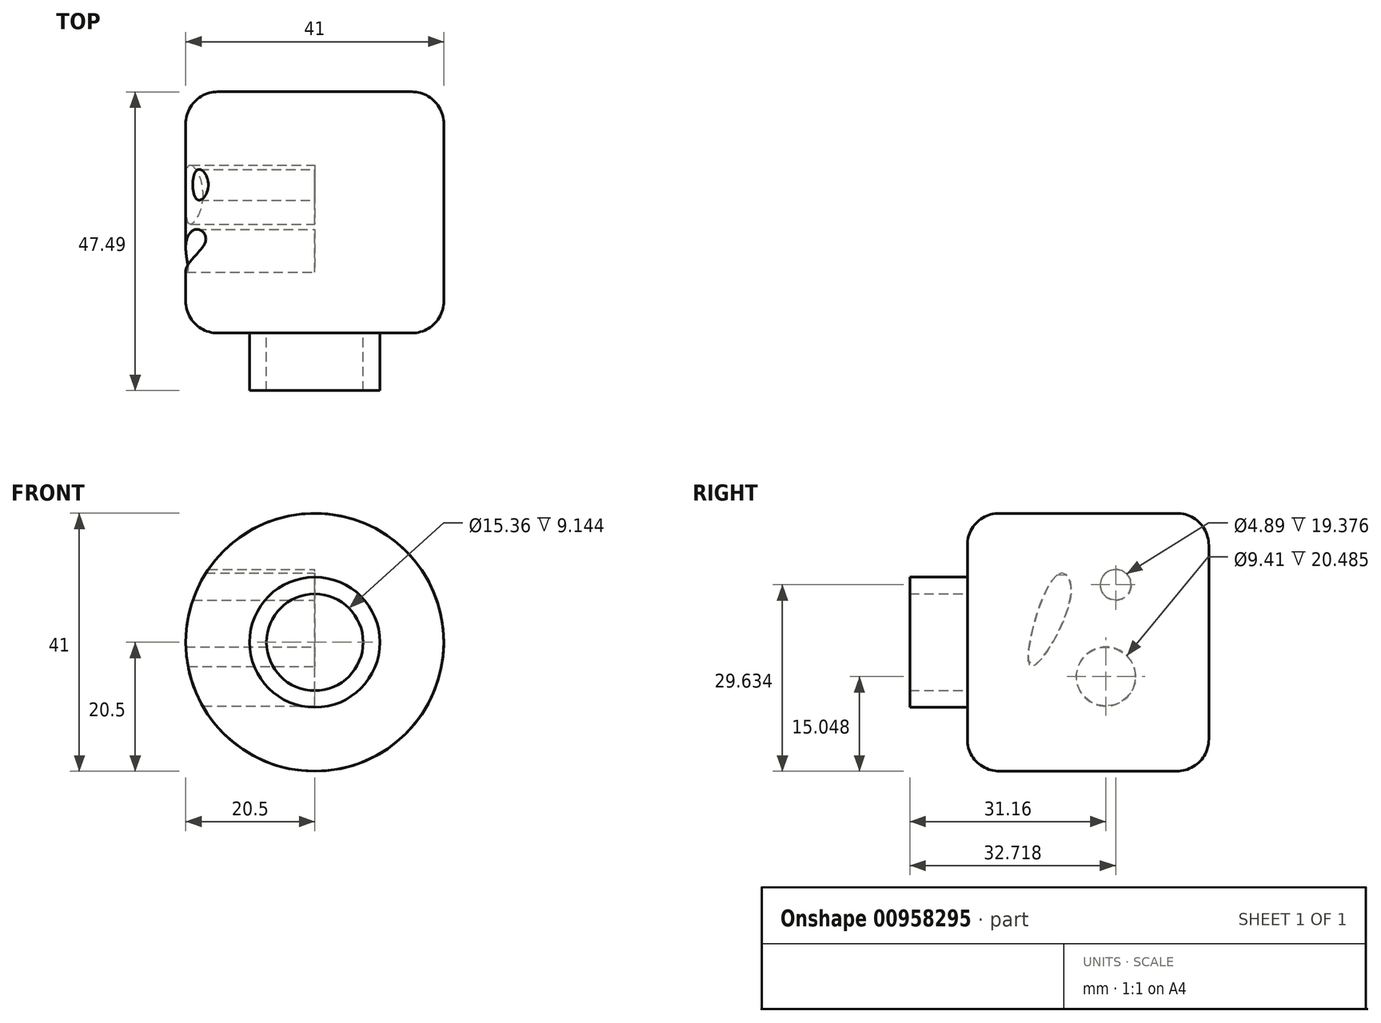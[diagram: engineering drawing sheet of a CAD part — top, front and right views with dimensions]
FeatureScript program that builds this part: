
annotation { "Feature Type Name" : "Feature", "Feature Type Description" : "" }
export const myFeature = defineFeature(function(context is Context, id is Id, definition is map)
    precondition{}
    {
        {
            var Q0;
            Q0=qCreatedBy(makeId("Front.planeOp"),FACE);
            var sketch = newSketch(context, id + "F0", { "sketchPlane" : qUnion([Q0])});
            skCircle(sketch, "E0", {"center": v(0, 0) * mm, "radius": 20.5 * mm});
            skSolve(sketch);
        }
        {
            var Q0;
            Q0=makeQuery(id+"F0.imprint","IMPRINT",FACE,{"disambiguationData":[TD([[makeQuery(id+"F0.imprint","IMPRINT",EDGE,{"derivedFrom":sQuery(id+"F0.wireOp",EDGE,"E0")}),1.0]])]});
            extrude(context, id + "F1", {"entities" : qUnion([Q0]), "oppositeDirection" : true, "depth" : 38.35 * mm, "offsetDistance" : 25.4 * mm});
        }
        {
            var Q0;
            Q0=makeQuery(id+"F1.opExtrude","CAP_EDGE",EDGE,{"disambiguationData":[OSD([sQuery(id+"F0.wireOp",EDGE,"E0")])],"isStart":true});
            var Q1;
            Q1=makeQuery(id+"F1.opExtrude","CAP_EDGE",EDGE,{"disambiguationData":[OSD([sQuery(id+"F0.wireOp",EDGE,"E0")])],"isStart":false});
            fillet(context, id + "F2", {"entities" : qUnion([Q0, Q1]), "radius" : 5.08 * mm, "tangentPropagation" : true, "allowEdgeOverflow" : false});
        }
        {
            var Q0;
            Q0=qCreatedBy(makeId("Front.planeOp"),FACE);
            var sketch = newSketch(context, id + "F3", { "sketchPlane" : qUnion([Q0])});
            skCircle(sketch, "E1", {"center": v(0, 0) * mm, "radius": 10.35 * mm});
            skSolve(sketch);
        }
        {
            var Q0;
            Q0 = qSketchRegion(id + "F3", true);
            extrude(context, id + "F4", {"entities" : qUnion([Q0]), "operationType" : NewBodyOperationType.ADD, "depth" : 9.14 * mm, "offsetDistance" : 25.4 * mm});
        }
        {
            var Q0;
            Q0=qCreatedBy(makeId("Front.planeOp"),FACE);
            var sketch = newSketch(context, id + "F5", { "sketchPlane" : qUnion([Q0])});
            skCircle(sketch, "E2", {"center": v(0, 0) * mm, "radius": 7.68 * mm});
            skSolve(sketch);
        }
        {
            var Q0;
            Q0 = qSketchRegion(id + "F5", true);
            var Q1;
            Q1=makeQuery(id+"F4.opExtrude","CAP_FACE",FACE,{"disambiguationData":[OSD([sQuery(id+"F3.wireOp",EDGE,"E1")])],"isStart":false});
            extrude(context, id + "F6", {"entities" : qUnion([Q0, Q1]), "operationType" : NewBodyOperationType.REMOVE, "depth" : 20.07 * mm, "offsetDistance" : 25.4 * mm});
        }
        {
            var Q0;
            Q0=qCreatedBy(makeId("Right.planeOp"),FACE);
            var sketch = newSketch(context, id + "F7", { "sketchPlane" : qUnion([Q0])});
            skCircle(sketch, "E3", {"center": v(23.58, 9.13) * mm, "radius": 2.44 * mm});
            skCircle(sketch, "E4", {"center": v(22.02, -5.45) * mm, "radius": 4.7 * mm});
            skFitSpline(sketch, "E5", {"points": [v(14.23, 10.7) * mm, v(9.98, -3.75) * mm, v(16.5, 8) * mm, v(14.23, 10.7) * mm]});
            skSolve(sketch);
        }
        {
            var Q0;
            Q0 = qSketchRegion(id + "F7", true);
            extrude(context, id + "F8", {"entities" : qUnion([Q0]), "operationType" : NewBodyOperationType.REMOVE, "oppositeDirection" : true, "depth" : 51.3 * mm, "offsetDistance" : 25.4 * mm});
        }
    });
